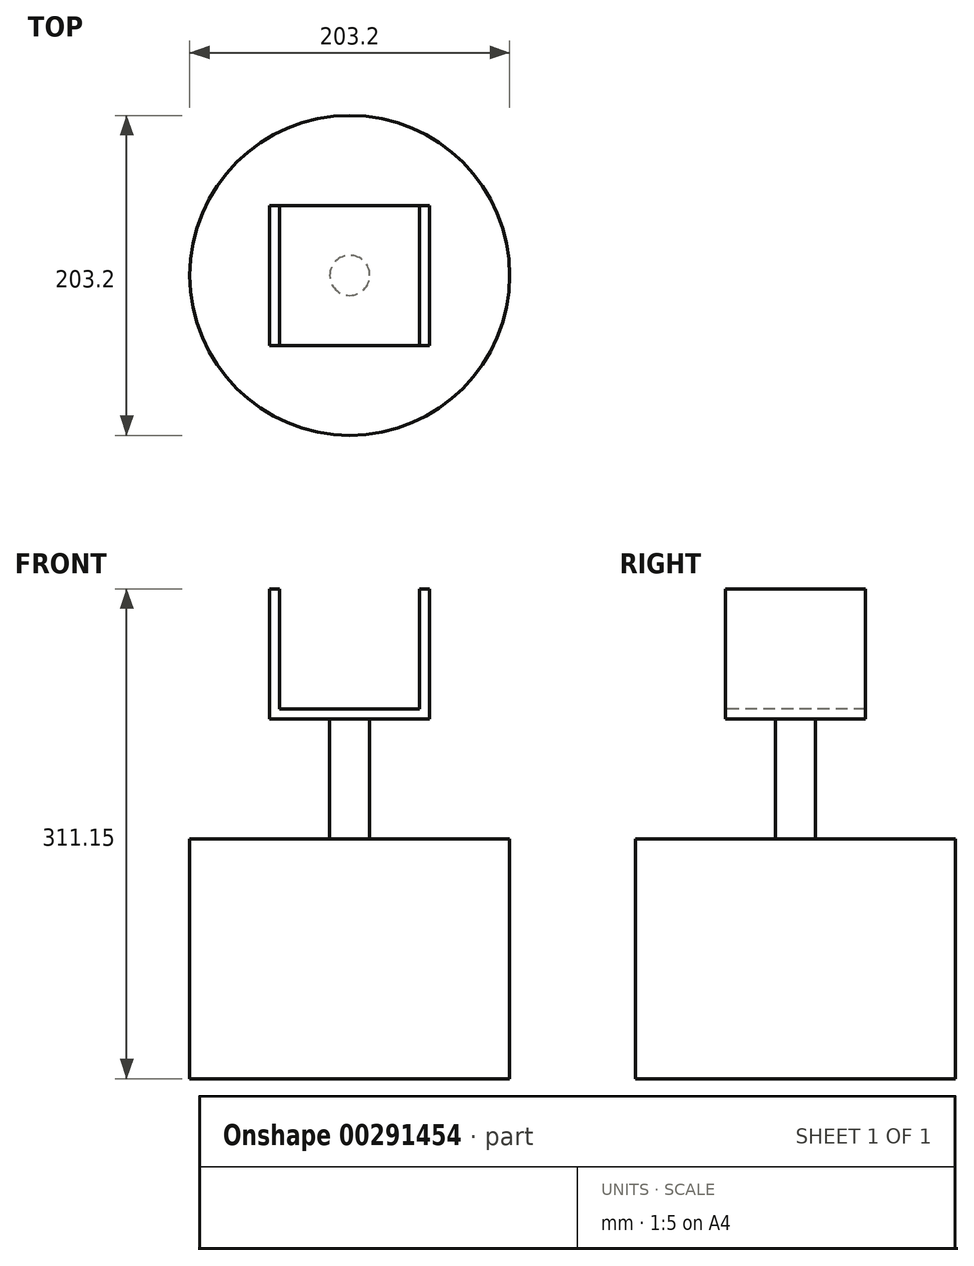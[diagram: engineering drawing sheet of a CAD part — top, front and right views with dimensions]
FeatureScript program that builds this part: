
annotation { "Feature Type Name" : "Feature", "Feature Type Description" : "" }
export const myFeature = defineFeature(function(context is Context, id is Id, definition is map)
    precondition{}
    {
        {
            var Q0;
            Q0=qCreatedBy(makeId("Top.planeOp"),FACE);
            var sketch = newSketch(context, id + "F0", { "sketchPlane" : qUnion([Q0])});
            skCircle(sketch, "E0", {"center": v(0, 0) * mm, "radius": 101.6 * mm});
            skSolve(sketch);
        }
        {
            var Q0;
            Q0=makeQuery(id+"F0.imprint","IMPRINT",FACE,{"disambiguationData":[TD([[makeQuery(id+"F0.imprint","IMPRINT",EDGE,{"derivedFrom":sQuery(id+"F0.wireOp",EDGE,"E0")}),1.0]])]});
            extrude(context, id + "F1", {"entities" : qUnion([Q0]), "depth" : 152.4 * mm});
        }
        {
            var Q0;
            Q0=makeQuery(id+"F1.opExtrude","CAP_FACE",FACE,{"disambiguationData":[OSD([sQuery(id+"F0.wireOp",EDGE,"E0")])],"isStart":false});
            var sketch = newSketch(context, id + "F2", { "sketchPlane" : qUnion([Q0])});
            skCircle(sketch, "E1", {"center": v(0, 0) * mm, "radius": 12.7 * mm});
            skSolve(sketch);
        }
        {
            var Q0;
            Q0=makeQuery(id+"F2.imprint","IMPRINT",FACE,{"disambiguationData":[TD([[makeQuery(id+"F2.imprint","IMPRINT",EDGE,{"derivedFrom":sQuery(id+"F2.wireOp",EDGE,"E1")}),1.0]])]});
            extrude(context, id + "F3", {"entities" : qUnion([Q0]), "operationType" : NewBodyOperationType.ADD, "depth" : 76.2 * mm});
        }
        {
            var Q0;
            Q0=makeQuery(id+"F3.opExtrude","CAP_FACE",FACE,{"disambiguationData":[OSD([sQuery(id+"F2.wireOp",EDGE,"E1")])],"isStart":false});
            var sketch = newSketch(context, id + "F4", { "sketchPlane" : qUnion([Q0])});
            skLineSegment(sketch, "E2.bottom", {"start": v(50.8, 44.45) * mm, "end": v(-50.8, 44.45) * mm});
            skLineSegment(sketch, "E2.top", {"start": v(50.8, -44.45) * mm, "end": v(-50.8, -44.45) * mm});
            skLineSegment(sketch, "E2.left", {"start": v(50.8, 44.45) * mm, "end": v(50.8, -44.45) * mm});
            skLineSegment(sketch, "E2.right", {"start": v(-50.8, 44.45) * mm, "end": v(-50.8, -44.45) * mm});
            skPoint(sketch, "E2.middle", {"position": v(0, 0) * mm});
            skSolve(sketch);
        }
        {
            var Q0;
            {var subQ0=sQuery(id+"F4.wireOp",EDGE,"K4epmSh5-EWmd-HBU6-rA8u-aSwJVVQLHfsW");Q0=makeQuery(id+"F4.imprint","IMPRINT",FACE,{"disambiguationData":[TD([[makeQuery(id+"F4.imprint","IMPRINT",EDGE,{"derivedFrom":subQ0}),1.0]])]});}
            var Q1;
            Q1=makeQuery(id+"F4.imprint","IMPRINT",FACE,{"disambiguationData":[TD([[makeQuery(id+"F4.imprint","IMPRINT",EDGE,{"derivedFrom":makeQuery(id+"F3.opExtrude","CAP_EDGE",EDGE,{"disambiguationData":[OSD([sQuery(id+"F2.wireOp",EDGE,"E1")])],"isStart":false})}),1.0]])]});
            var Q2;
            {var subQ0=sQuery(id+"F4.wireOp",EDGE,"E2.right");Q2=makeQuery(id+"F4.imprint","IMPRINT",FACE,{"disambiguationData":[TD([[makeQuery(id+"F4.imprint","IMPRINT",EDGE,{"derivedFrom":subQ0}),1.0]])]});}
            var Q3;
            {var subQ0=sQuery(id+"F4.wireOp",EDGE,"E2.left");Q3=makeQuery(id+"F4.imprint","IMPRINT",FACE,{"disambiguationData":[TD([[makeQuery(id+"F4.imprint","IMPRINT",EDGE,{"derivedFrom":subQ0}),-1.0]])]});}
            extrude(context, id + "F5", {"entities" : qUnion([Q0, Q1, Q2, Q3]), "operationType" : NewBodyOperationType.ADD, "depth" : 6.35 * mm});
        }
        {
            var Q0;
            Q0=makeQuery(id+"F5.opExtrude","CAP_FACE",FACE,{"disambiguationData":[OSD([sQuery(id+"F4.wireOp",EDGE,"E2.bottom"),sQuery(id+"F4.wireOp",EDGE,"E2.top"),sQuery(id+"F4.wireOp",EDGE,"E2.left"),sQuery(id+"F4.wireOp",EDGE,"E2.right")])],"isStart":false});
            var sketch = newSketch(context, id + "F6", { "sketchPlane" : qUnion([Q0])});
            skLineSegment(sketch, "E3", {"start": v(-44.45, 44.45) * mm, "end": v(-44.45, -44.45) * mm});
            skLineSegment(sketch, "E4", {"start": v(44.45, 44.45) * mm, "end": v(44.45, -44.45) * mm});
            skSolve(sketch);
        }
        {
            var Q0;
            {var subQ0=sQuery(id+"F6.wireOp",EDGE,"E3");Q0=makeQuery(id+"F6.imprint","IMPRINT",FACE,{"disambiguationData":[TD([[makeQuery(id+"F6.imprint","IMPRINT",EDGE,{"derivedFrom":subQ0}),-1.0]])]});}
            var Q1;
            {var subQ0=sQuery(id+"F6.wireOp",EDGE,"E4");Q1=makeQuery(id+"F6.imprint","IMPRINT",FACE,{"disambiguationData":[TD([[makeQuery(id+"F6.imprint","IMPRINT",EDGE,{"derivedFrom":subQ0}),1.0]])]});}
            extrude(context, id + "F7", {"entities" : qUnion([Q0, Q1]), "operationType" : NewBodyOperationType.ADD, "depth" : 76.2 * mm});
        }
    });
